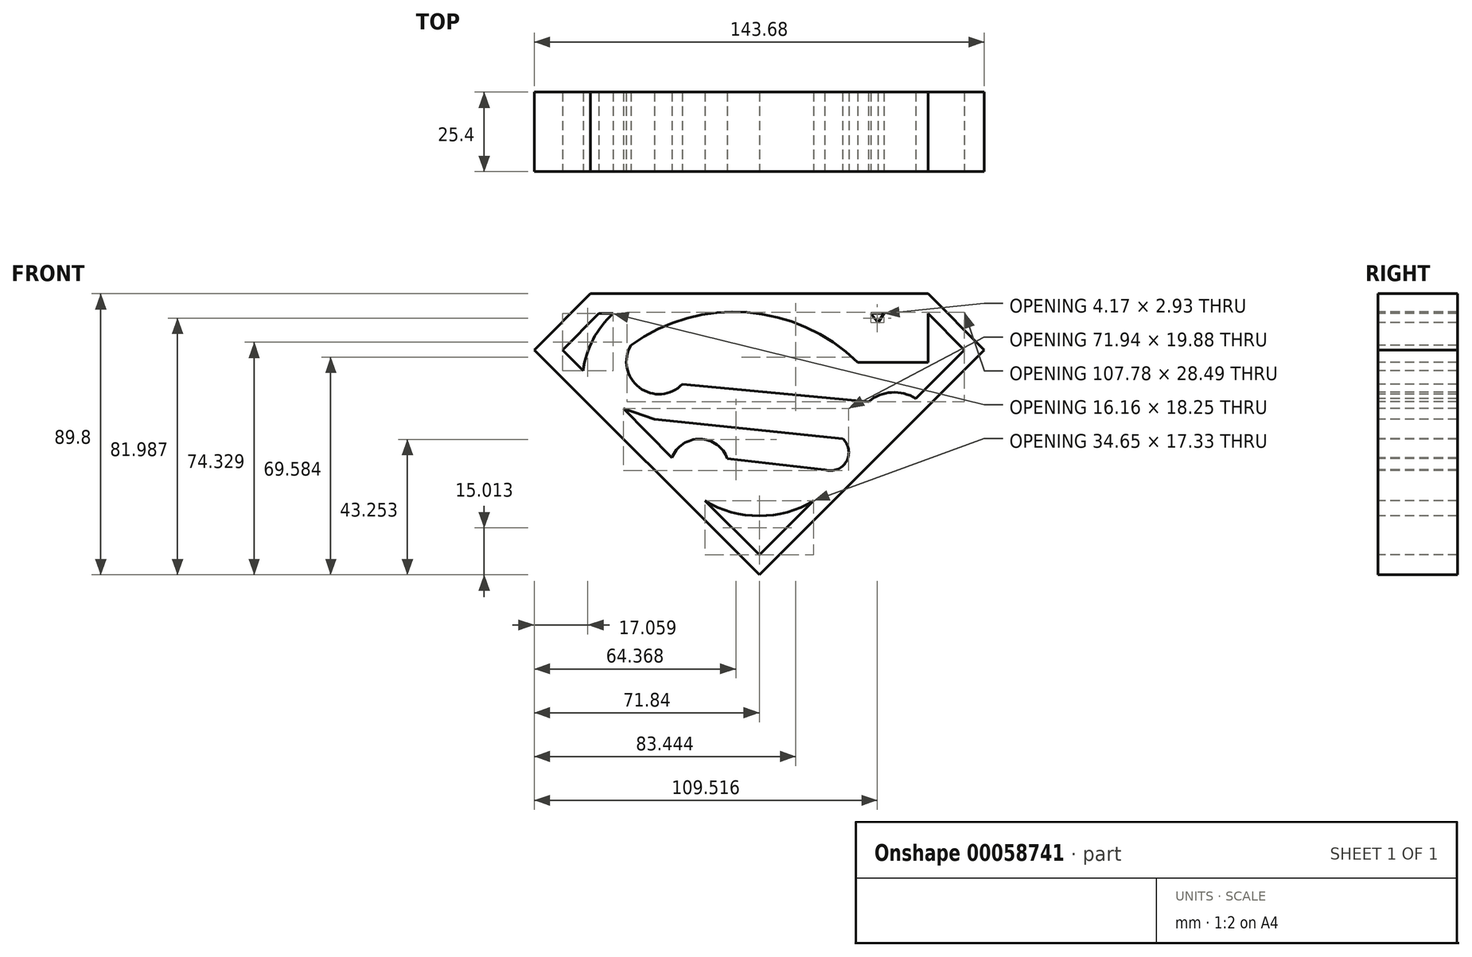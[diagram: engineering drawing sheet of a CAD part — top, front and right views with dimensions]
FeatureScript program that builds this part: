
annotation { "Feature Type Name" : "Feature", "Feature Type Description" : "" }
export const myFeature = defineFeature(function(context is Context, id is Id, definition is map)
    precondition{}
    {
        {
            var Q0;
            Q0=qCreatedBy(makeId("Front.planeOp"),FACE);
            var sketch = newSketch(context, id + "F0", { "sketchPlane" : qUnion([Q0])});
            skLineSegment(sketch, "E0", {"start": v(0, 0) * mm, "end": v(-71.84, 71.84) * mm});
            skLineSegment(sketch, "E1", {"start": v(0, 0) * mm, "end": v(71.84, 71.84) * mm});
            skLineSegment(sketch, "E2", {"start": v(-71.84, 71.84) * mm, "end": v(-53.88, 89.8) * mm});
            skLineSegment(sketch, "E3", {"start": v(71.84, 71.84) * mm, "end": v(53.88, 89.8) * mm});
            skLineSegment(sketch, "E4", {"start": v(53.88, 89.8) * mm, "end": v(-53.88, 89.8) * mm});
            skLineSegment(sketch, "E5", {"start": v(0, 6.35) * mm, "end": v(-17.33, 23.68) * mm});
            skLineSegment(sketch, "E6", {"start": v(0, 6.35) * mm, "end": v(17.33, 23.68) * mm});
            skArc(sketch, "E7", {"start": v(-17.33, 23.68) * mm, "mid": v(0, 18.84) * mm, "end": v(17.33, 23.68) * mm});
            skLineSegment(sketch, "E8", {"start": v(-56.23, 65.2) * mm, "end": v(-62.86, 71.84) * mm});
            skLineSegment(sketch, "E9", {"start": v(-62.86, 71.84) * mm, "end": v(-51.25, 83.45) * mm});
            skLineSegment(sketch, "E10", {"start": v(-51.25, 83.45) * mm, "end": v(-46.7, 83.45) * mm});
            skArc(sketch, "E11", {"start": v(-46.7, 83.45) * mm, "mid": v(-53.09, 75.18) * mm, "end": v(-56.23, 65.2) * mm});
            skLineSegment(sketch, "E12", {"start": v(35.6, 83.45) * mm, "end": v(37.85, 80.52) * mm});
            skLineSegment(sketch, "E13", {"start": v(37.85, 80.52) * mm, "end": v(39.76, 83.45) * mm});
            skLineSegment(sketch, "E14", {"start": v(39.76, 83.45) * mm, "end": v(35.6, 83.45) * mm});
            skLineSegment(sketch, "E15", {"start": v(53.88, 83.45) * mm, "end": v(65.5, 71.84) * mm});
            skLineSegment(sketch, "E16", {"start": v(53.88, 83.45) * mm, "end": v(53.88, 67.93) * mm});
            skLineSegment(sketch, "E17", {"start": v(53.88, 67.93) * mm, "end": v(31.4, 67.93) * mm});
            skArc(sketch, "E18", {"start": v(31.4, 67.93) * mm, "mid": v(-3.82, 83.83) * mm, "end": v(-41, 73.35) * mm});
            skArc(sketch, "E19", {"start": v(-41, 73.35) * mm, "mid": v(-38.32, 59.83) * mm, "end": v(-24.58, 60.91) * mm});
            skLineSegment(sketch, "E20", {"start": v(-43.44, 53.2) * mm, "end": v(-27.89, 37.37) * mm});
            skLineSegment(sketch, "E21", {"start": v(-43.44, 53.2) * mm, "end": v(-33.52, 49.7) * mm});
            skLineSegment(sketch, "E22", {"start": v(65.5, 71.84) * mm, "end": v(49.97, 56.32) * mm});
            skLineSegment(sketch, "E23", {"start": v(-24.58, 60.91) * mm, "end": v(34.86, 55.34) * mm});
            skArc(sketch, "E24", {"start": v(49.97, 56.32) * mm, "mid": v(42.26, 58.26) * mm, "end": v(34.86, 55.34) * mm});
            skLineSegment(sketch, "E25", {"start": v(-33.52, 49.7) * mm, "end": v(26.55, 43.54) * mm});
            skArc(sketch, "E26", {"start": v(20.92, 33.62) * mm, "mid": v(27.83, 36.25) * mm, "end": v(26.55, 43.54) * mm});
            skLineSegment(sketch, "E27", {"start": v(20.92, 33.62) * mm, "end": v(-10.2, 37.1) * mm});
            skArc(sketch, "E28", {"start": v(-10.2, 37.1) * mm, "mid": v(-18.95, 43.4) * mm, "end": v(-27.89, 37.37) * mm});
            skSolve(sketch);
        }
        {
            var Q0;
            Q0=makeQuery(id+"F0.imprint","IMPRINT",FACE,{"disambiguationData":[TD([[makeQuery(id+"F0.imprint","IMPRINT",EDGE,{"derivedFrom":sQuery(id+"F0.wireOp",EDGE,"E0")}),-1.0]])]});
            extrude(context, id + "F1", {"entities" : qUnion([Q0]), "oppositeDirection" : true, "depth" : 25.4 * mm});
        }
    });
